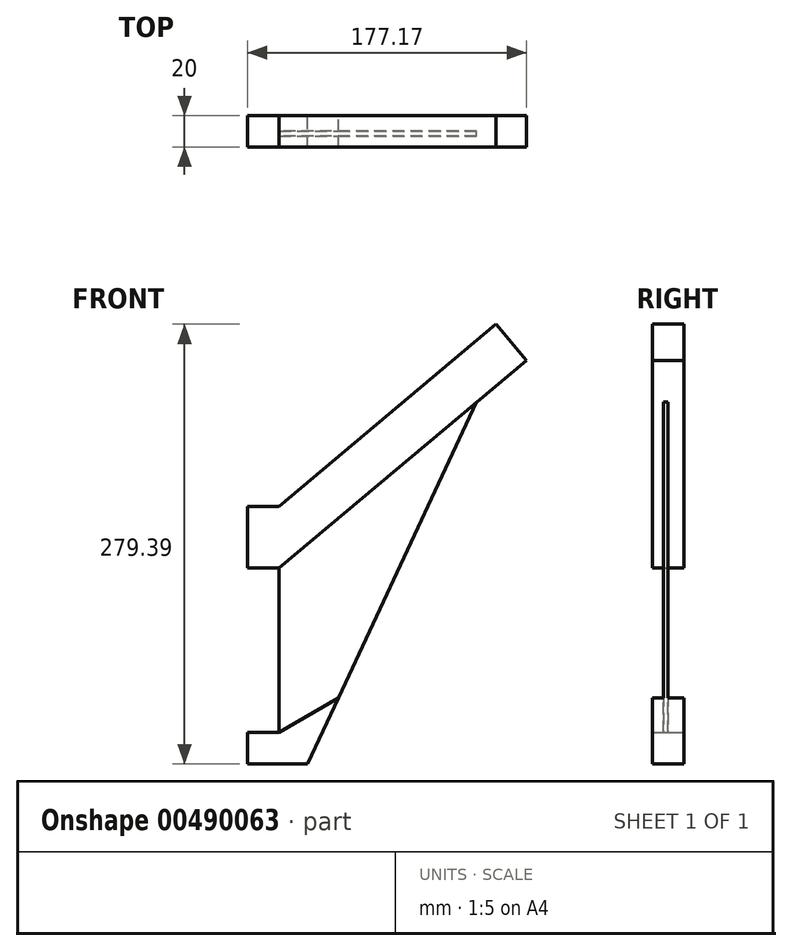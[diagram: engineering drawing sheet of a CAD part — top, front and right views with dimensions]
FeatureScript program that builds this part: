
annotation { "Feature Type Name" : "Feature", "Feature Type Description" : "" }
export const myFeature = defineFeature(function(context is Context, id is Id, definition is map)
    precondition{}
    {
        {
            var Q0;
            Q0=qCreatedBy(makeId("Front.planeOp"),FACE);
            var sketch = newSketch(context, id + "F0", { "sketchPlane" : qUnion([Q0])});
            skLineSegment(sketch, "E0", {"start": v(-29.12, 39.16) * mm, "end": v(-9.12, 39.16) * mm});
            skLineSegment(sketch, "E1", {"start": v(-9.12, 39.16) * mm, "end": v(128.77, 154.86) * mm});
            skLineSegment(sketch, "E2", {"start": v(128.77, 154.86) * mm, "end": v(148.05, 131.88) * mm});
            skLineSegment(sketch, "E3", {"start": v(148.05, 131.88) * mm, "end": v(-9.12, 0) * mm});
            skLineSegment(sketch, "E4", {"start": v(-9.12, 0) * mm, "end": v(-9.12, -104.53) * mm});
            skLineSegment(sketch, "E5", {"start": v(-9.12, -104.53) * mm, "end": v(-29.12, -104.53) * mm});
            skLineSegment(sketch, "E6", {"start": v(-29.12, -104.53) * mm, "end": v(-29.12, -124.53) * mm});
            skLineSegment(sketch, "E7", {"start": v(-29.12, -124.53) * mm, "end": v(9.07, -124.53) * mm});
            skLineSegment(sketch, "E8", {"start": v(9.07, -124.53) * mm, "end": v(116.33, 105.27) * mm});
            skLineSegment(sketch, "E9", {"start": v(-29.12, 39.16) * mm, "end": v(-29.12, 0) * mm});
            skLineSegment(sketch, "E10", {"start": v(-29.12, 0) * mm, "end": v(-9.12, 0) * mm});
            skLineSegment(sketch, "E11", {"start": v(-9.12, -104.53) * mm, "end": v(28.62, -82.65) * mm});
            skSolve(sketch);
        }
        {
            var Q0;
            Q0=makeQuery(id+"F0.imprint","IMPRINT",FACE,{"disambiguationData":[TD([[makeQuery(id+"F0.imprint","IMPRINT",EDGE,{"derivedFrom":sQuery(id+"F0.wireOp",EDGE,"E0")}),-1.0]])]});
            extrude(context, id + "F1", {"entities" : qUnion([Q0]), "depth" : 10 * mm, "hasSecondDirection" : true, "secondDirectionOppositeDirection" : true, "secondDirectionDepth" : 10 * mm});
        }
        {
            var Q0;
            {var subQ0=sQuery(id+"F0.wireOp",EDGE,"E4");Q0=makeQuery(id+"F0.imprint","IMPRINT",FACE,{"disambiguationData":[TD([[makeQuery(id+"F0.imprint","IMPRINT",EDGE,{"derivedFrom":subQ0}),1.0]])]});}
            extrude(context, id + "F2", {"entities" : qUnion([Q0]), "operationType" : NewBodyOperationType.ADD, "depth" : 3 * mm});
        }
        {
            var Q0;
            Q0=makeQuery(id+"F0.imprint","IMPRINT",FACE,{"disambiguationData":[TD([[makeQuery(id+"F0.imprint","IMPRINT",EDGE,{"derivedFrom":sQuery(id+"F0.wireOp",EDGE,"E5")}),1.0]])]});
            extrude(context, id + "F3", {"entities" : qUnion([Q0]), "operationType" : NewBodyOperationType.ADD, "depth" : 10 * mm, "hasSecondDirection" : true, "secondDirectionOppositeDirection" : true, "secondDirectionDepth" : 10 * mm});
        }
    });
